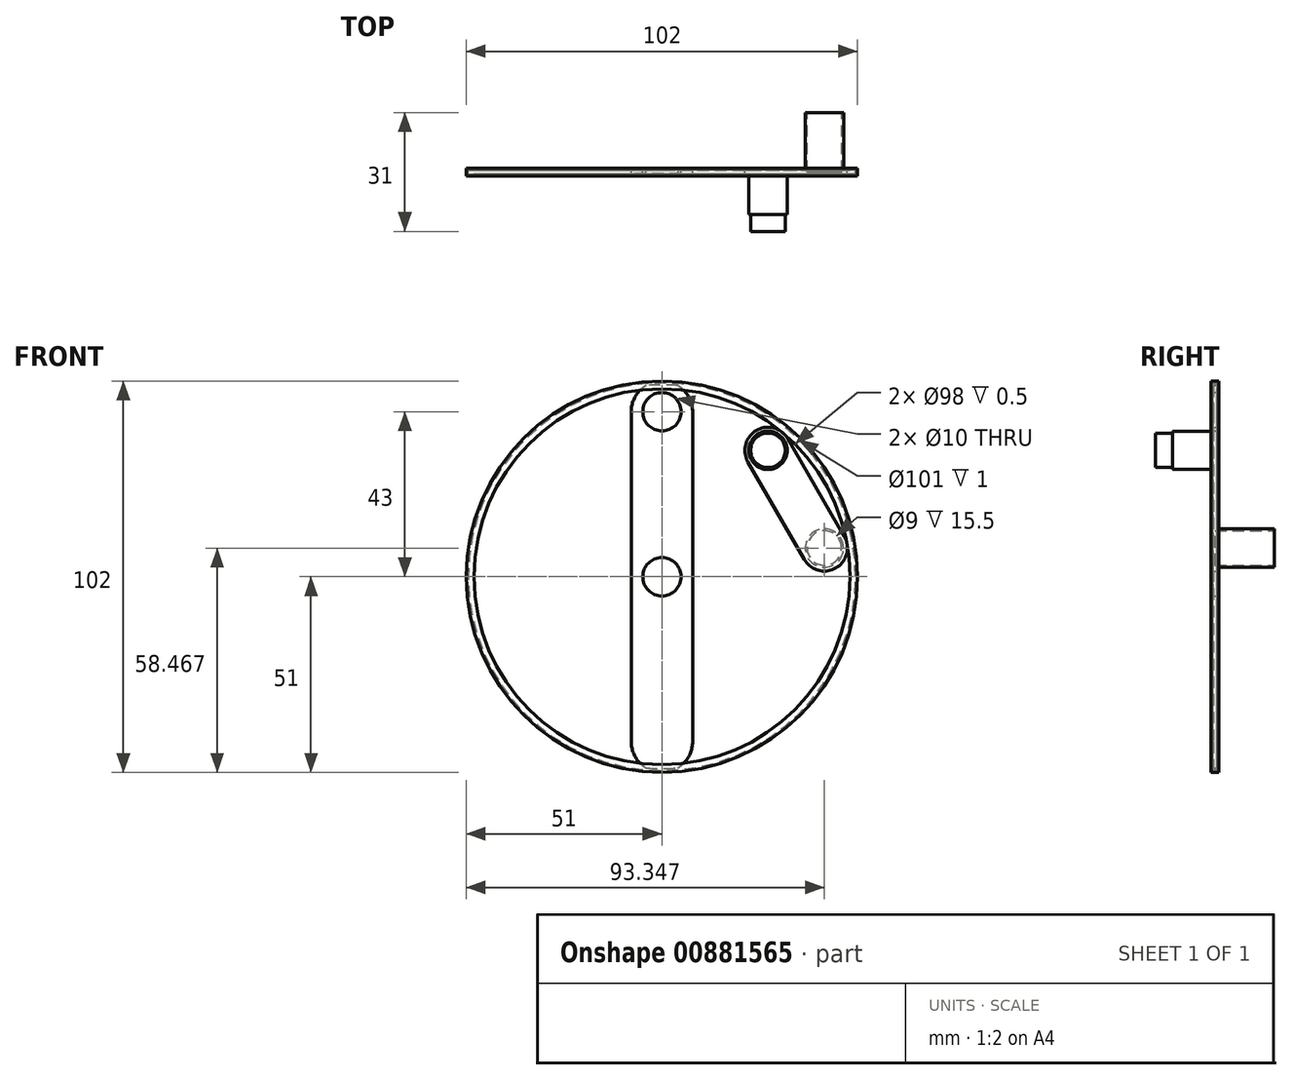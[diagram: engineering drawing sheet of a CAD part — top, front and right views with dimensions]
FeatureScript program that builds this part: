
annotation { "Feature Type Name" : "Feature", "Feature Type Description" : "" }
export const myFeature = defineFeature(function(context is Context, id is Id, definition is map)
    precondition{}
    {
        {
            var Q0;
            Q0=qCreatedBy(makeId("Front.planeOp"),FACE);
            var sketch = newSketch(context, id + "F0", { "sketchPlane" : qUnion([Q0])});
            skCircle(sketch, "E0", {"center": v(0, 0) * mm, "radius": 50 * mm});
            skArc(sketch, "E1", {"start": v(5, 0) * mm, "mid": v(0, 5) * mm, "end": v(-5, 0) * mm});
            skLineSegment(sketch, "E2", {"start": v(0, 0) * mm, "end": v(0, 50) * mm, "construction": true});
            skLineSegment(sketch, "E3", {"start": v(50, 0) * mm, "end": v(0, 0) * mm, "construction": true});
            skCircle(sketch, "E4", {"center": v(0, 43) * mm, "radius": 5 * mm});
            skCircle(sketch, "E5.1.0", {"center": v(-27.64, 32.94) * mm, "radius": 5 * mm});
            skCircle(sketch, "E5.2.0", {"center": v(-42.35, 7.47) * mm, "radius": 5 * mm});
            skCircle(sketch, "E6.1.3.0", {"center": v(-37.24, -21.5) * mm, "radius": 5 * mm});
            skCircle(sketch, "E6.1.4.0", {"center": v(-14.7, -40.4) * mm, "radius": 5 * mm});
            skCircle(sketch, "E6.1.5.0", {"center": v(14.7, -40.4) * mm, "radius": 5 * mm});
            skCircle(sketch, "E6.1.6.0", {"center": v(37.24, -21.5) * mm, "radius": 5 * mm});
            skCircle(sketch, "E6.1.7.0", {"center": v(42.35, 7.47) * mm, "radius": 5 * mm});
            skCircle(sketch, "E6.1.8.0", {"center": v(27.64, 32.94) * mm, "radius": 5 * mm});
            skArc(sketch, "E7.0", {"start": v(-4.17, 49.83) * mm, "mid": v(-6.98, 46.91) * mm, "end": v(-8, 43) * mm});
            skLineSegment(sketch, "E8.0", {"start": v(-8, 0) * mm, "end": v(-8, 0) * mm});
            skLineSegment(sketch, "E9", {"start": v(-8, 43) * mm, "end": v(-8, 0) * mm});
            skLineSegment(sketch, "E10", {"start": v(8, 43) * mm, "end": v(8, 0) * mm});
            skArc(sketch, "E11.trimOffspring", {"start": v(8, 43) * mm, "mid": v(6.98, 46.91) * mm, "end": v(4.17, 49.83) * mm});
            skLineSegment(sketch, "E12", {"start": v(0, 0) * mm, "end": v(-50, 0) * mm, "construction": true});
            skArc(sketch, "E13.MirrorCS", {"start": v(5, 0) * mm, "mid": v(0, -5) * mm, "end": v(-5, 0) * mm});
            skLineSegment(sketch, "E14.MirrorCS", {"start": v(-8, -43) * mm, "end": v(-8, 0) * mm});
            skLineSegment(sketch, "E15.MirrorCS", {"start": v(8, -43) * mm, "end": v(8, 0) * mm});
            skArc(sketch, "E16.MirrorCS", {"start": v(8, -43) * mm, "mid": v(6.98, -46.91) * mm, "end": v(4.17, -49.83) * mm});
            skArc(sketch, "E17.MirrorCS", {"start": v(-4.17, -49.83) * mm, "mid": v(-6.98, -46.91) * mm, "end": v(-8, -43) * mm});
            skCircle(sketch, "E18.0", {"center": v(27.64, 32.94) * mm, "radius": 6 * mm});
            skCircle(sketch, "E19.0", {"center": v(42.35, 7.47) * mm, "radius": 6 * mm});
            skLineSegment(sketch, "E20", {"start": v(22.44, 29.94) * mm, "end": v(37.15, 4.47) * mm});
            skLineSegment(sketch, "E21", {"start": v(47.54, 10.47) * mm, "end": v(32.84, 35.94) * mm});
            skCircle(sketch, "E22.0", {"center": v(0, 0) * mm, "radius": 49 * mm});
            skCircle(sketch, "E23.0", {"center": v(0, 0) * mm, "radius": 51 * mm});
            skSolve(sketch);
        }
        {
            var Q0;
            {var subQ0=sQuery(id+"F0.wireOp",EDGE,"E7.0");var subQ1=sQuery(id+"F0.wireOp",EDGE,"E0");var subQ2=makeQuery(id+"F0.imprint","INTERSECT",VERTEX,{"derivedFrom":[subQ1,subQ0]});Q0=makeQuery(id+"F0.imprint","IMPRINT",FACE,{"disambiguationData":[TD([[makeQuery(id+"F0.imprint","IMPRINT",EDGE,{"disambiguationData":[TD([[subQ2,1.0]])],"derivedFrom":subQ1}),1.0]])]});}
            var Q1;
            Q1=makeQuery(id+"F0.imprint","IMPRINT",FACE,{"disambiguationData":[TD([[makeQuery(id+"F0.imprint","IMPRINT",EDGE,{"derivedFrom":sQuery(id+"F0.wireOp",EDGE,"E1")}),-1.0]])]});
            var Q2;
            {var subQ0=sQuery(id+"F0.wireOp",EDGE,"E16.MirrorCS");var subQ1=sQuery(id+"F0.wireOp",EDGE,"E0");var subQ2=makeQuery(id+"F0.imprint","INTERSECT",VERTEX,{"derivedFrom":[subQ1,subQ0]});Q2=makeQuery(id+"F0.imprint","IMPRINT",FACE,{"disambiguationData":[TD([[makeQuery(id+"F0.imprint","IMPRINT",EDGE,{"disambiguationData":[TD([[subQ2,1.0]])],"derivedFrom":subQ1}),1.0]])]});}
            extrude(context, id + "F1", {"entities" : qUnion([Q0, Q1, Q2]), "depth" : 0.9 * mm, "offsetDistance" : 25 * mm});
        }
        {
            var Q0;
            Q0=makeQuery(id+"F0.imprint","IMPRINT",FACE,{"disambiguationData":[TD([[makeQuery(id+"F0.imprint","IMPRINT",EDGE,{"derivedFrom":sQuery(id+"F0.wireOp",EDGE,"E23.0")}),1.0]])]});
            var Q1;
            {var subQ0=sQuery(id+"F0.wireOp",EDGE,"E7.0");var subQ1=sQuery(id+"F0.wireOp",EDGE,"E0");var subQ2=makeQuery(id+"F0.imprint","INTERSECT",VERTEX,{"derivedFrom":[subQ1,subQ0]});Q1=makeQuery(id+"F0.imprint","IMPRINT",FACE,{"disambiguationData":[TD([[makeQuery(id+"F0.imprint","IMPRINT",EDGE,{"disambiguationData":[TD([[subQ2,-1.0]])],"derivedFrom":subQ1}),1.0]])]});}
            var Q2;
            {var subQ0=sQuery(id+"F0.wireOp",EDGE,"E7.0");var subQ1=sQuery(id+"F0.wireOp",EDGE,"E0");var subQ2=makeQuery(id+"F0.imprint","INTERSECT",VERTEX,{"derivedFrom":[subQ1,subQ0]});Q2=makeQuery(id+"F0.imprint","IMPRINT",FACE,{"disambiguationData":[TD([[makeQuery(id+"F0.imprint","IMPRINT",EDGE,{"disambiguationData":[TD([[subQ2,1.0]])],"derivedFrom":subQ1}),1.0]])]});}
            var Q3;
            {var subQ4=sQuery(id+"F0.wireOp",EDGE,"E0");var subQ7=sQuery(id+"F0.wireOp",EDGE,"E11.trimOffspring");var subQ8=makeQuery(id+"F0.imprint","INTERSECT",VERTEX,{"derivedFrom":[subQ4,subQ7]});Q3=makeQuery(id+"F0.imprint","IMPRINT",FACE,{"disambiguationData":[TD([[makeQuery(id+"F0.imprint","IMPRINT",EDGE,{"disambiguationData":[TD([[subQ8,1.0]])],"derivedFrom":subQ4}),1.0]])]});}
            var Q4;
            {var subQ0=sQuery(id+"F0.wireOp",EDGE,"E16.MirrorCS");var subQ1=sQuery(id+"F0.wireOp",EDGE,"E0");var subQ2=makeQuery(id+"F0.imprint","INTERSECT",VERTEX,{"derivedFrom":[subQ1,subQ0]});Q4=makeQuery(id+"F0.imprint","IMPRINT",FACE,{"disambiguationData":[TD([[makeQuery(id+"F0.imprint","IMPRINT",EDGE,{"disambiguationData":[TD([[subQ2,1.0]])],"derivedFrom":subQ1}),1.0]])]});}
            extrude(context, id + "F2", {"entities" : qUnion([Q0, Q1, Q2, Q3, Q4]), "depth" : 1.5 * mm, "offsetDistance" : 25 * mm, "hasSecondDirection" : true, "secondDirectionOppositeDirection" : true, "secondDirectionDepth" : 0.5 * mm});
        }
        {
            var Q0;
            Q0=makeQuery(id+"F2.opExtrude","SWEPT_FACE",FACE,{"disambiguationData":[OSD([sQuery(id+"F0.wireOp",EDGE,"E22.0")])]});
            shell(context, id + "F3", {"entities" : qUnion([Q0]), "thickness" : 0.5 * mm});
        }
        {
            var Q0;
            Q0=makeQuery(id+"F0.imprint","IMPRINT",FACE,{"disambiguationData":[TD([[makeQuery(id+"F0.imprint","IMPRINT",EDGE,{"derivedFrom":sQuery(id+"F0.wireOp",EDGE,"E6.1.8.0")}),-1.0]])]});
            var Q1;
            {var subQ0=sQuery(id+"F0.wireOp",EDGE,"E20");Q1=makeQuery(id+"F0.imprint","IMPRINT",FACE,{"disambiguationData":[TD([[makeQuery(id+"F0.imprint","IMPRINT",EDGE,{"derivedFrom":subQ0}),1.0]])]});}
            var Q2;
            Q2=makeQuery(id+"F0.imprint","IMPRINT",FACE,{"disambiguationData":[TD([[makeQuery(id+"F0.imprint","IMPRINT",EDGE,{"derivedFrom":sQuery(id+"F0.wireOp",EDGE,"E6.1.7.0")}),-1.0]])]});
            extrude(context, id + "F4", {"entities" : qUnion([Q0, Q1, Q2]), "depth" : 1 * mm, "offsetDistance" : 25 * mm});
        }
        {
            var Q0;
            Q0=makeQuery(id+"F0.imprint","IMPRINT",FACE,{"disambiguationData":[TD([[makeQuery(id+"F0.imprint","IMPRINT",EDGE,{"derivedFrom":sQuery(id+"F0.wireOp",EDGE,"E6.1.8.0")}),1.0]])]});
            extrude(context, id + "F5", {"entities" : qUnion([Q0]), "operationType" : NewBodyOperationType.ADD, "depth" : 16 * mm, "offsetDistance" : 25 * mm});
        }
        {
            var Q0;
            Q0=makeQuery(id+"F0.imprint","IMPRINT",FACE,{"disambiguationData":[TD([[makeQuery(id+"F0.imprint","IMPRINT",EDGE,{"derivedFrom":sQuery(id+"F0.wireOp",EDGE,"E6.1.7.0")}),1.0]])]});
            extrude(context, id + "F6", {"entities" : qUnion([Q0]), "operationType" : NewBodyOperationType.ADD, "depth" : 1 * mm, "offsetDistance" : 25 * mm, "hasSecondDirection" : true, "secondDirectionOppositeDirection" : true, "secondDirectionDepth" : 15 * mm});
        }
        {
            var Q0;
            Q0=makeQuery(id+"F6.opExtrude","CAP_FACE",FACE,{"disambiguationData":[OSD([sQuery(id+"F0.wireOp",EDGE,"E6.1.7.0")])],"isStart":true});
            shell(context, id + "F7", {"entities" : qUnion([Q0]), "thickness" : 0.5 * mm});
        }
        {
            var Q0;
            Q0=makeQuery(id+"F5.opExtrude","CAP_FACE",FACE,{"disambiguationData":[OSD([sQuery(id+"F0.wireOp",EDGE,"E6.1.8.0")])],"isStart":false});
            var sketch = newSketch(context, id + "F8", { "sketchPlane" : qUnion([Q0])});
            skCircle(sketch, "E24", {"center": v(27.64, 32.94) * mm, "radius": 4.5 * mm});
            skCircle(sketch, "E25", {"center": v(27.64, 32.94) * mm, "radius": 5 * mm});
            skSolve(sketch);
        }
        {
            var Q0;
            Q0=makeQuery(id+"F8.imprint","IMPRINT",FACE,{"disambiguationData":[TD([[makeQuery(id+"F8.imprint","IMPRINT",EDGE,{"derivedFrom":sQuery(id+"F8.wireOp",EDGE,"E24")}),1.0]])]});
            extrude(context, id + "F9", {"entities" : qUnion([Q0]), "operationType" : NewBodyOperationType.ADD, "oppositeDirection" : true, "depth" : 16 * mm, "offsetDistance" : 25 * mm});
        }
        {
            var Q0;
            Q0=makeQuery(id+"F8.imprint","IMPRINT",FACE,{"disambiguationData":[TD([[makeQuery(id+"F8.imprint","IMPRINT",EDGE,{"derivedFrom":sQuery(id+"F8.wireOp",EDGE,"E24")}),-1.0]])]});
            extrude(context, id + "F10", {"entities" : qUnion([Q0]), "operationType" : NewBodyOperationType.REMOVE, "oppositeDirection" : true, "depth" : 4.4 * mm, "offsetDistance" : 25 * mm});
        }
    });
